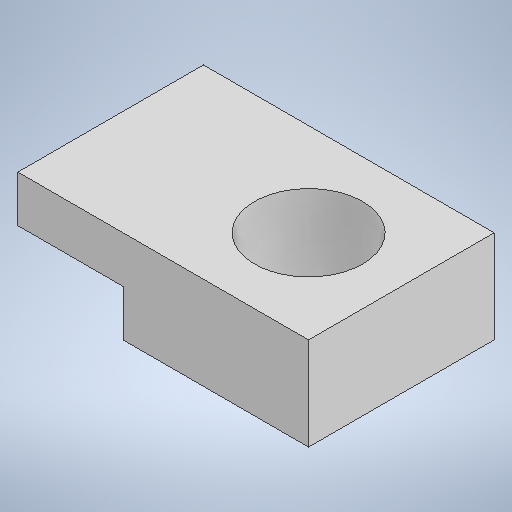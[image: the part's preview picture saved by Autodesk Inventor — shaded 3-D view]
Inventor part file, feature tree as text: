
AUTODESK INVENTOR PART (.ipt)
format: ipt  version: 2025 (Build 290162000, 162)  size: 199,168 bytes
history: native  units: in
note: dims shown in document units (in); Inventor stores cm internally (conversion verified against a paired STEP export)
features: extrude x2, sketch x2, projected_geometry x1
ambient origin geometry x8: Origin, YZ Plane, XZ Plane, XY Plane, X Axis, Y Axis, Z Axis, Center Point
bodies: Solid1 (feature_tree)
feature tree (5):
  extrude  "Extrusion1"  Depth=0.2362in
  extrude  "Extrusion2"  Depth=0.0591in TaperAngle=0.0deg
  sketch  "Sketch1"  dims[d0=0.2362in d1=0.2362in]
  sketch  "Sketch2"  dims[d2=0.1378in d3=0.0591in d4=0.0in d5=0.1339in d6=0.0591in d7=0.0in]
  projected_geometry  "Projected Loop1"
